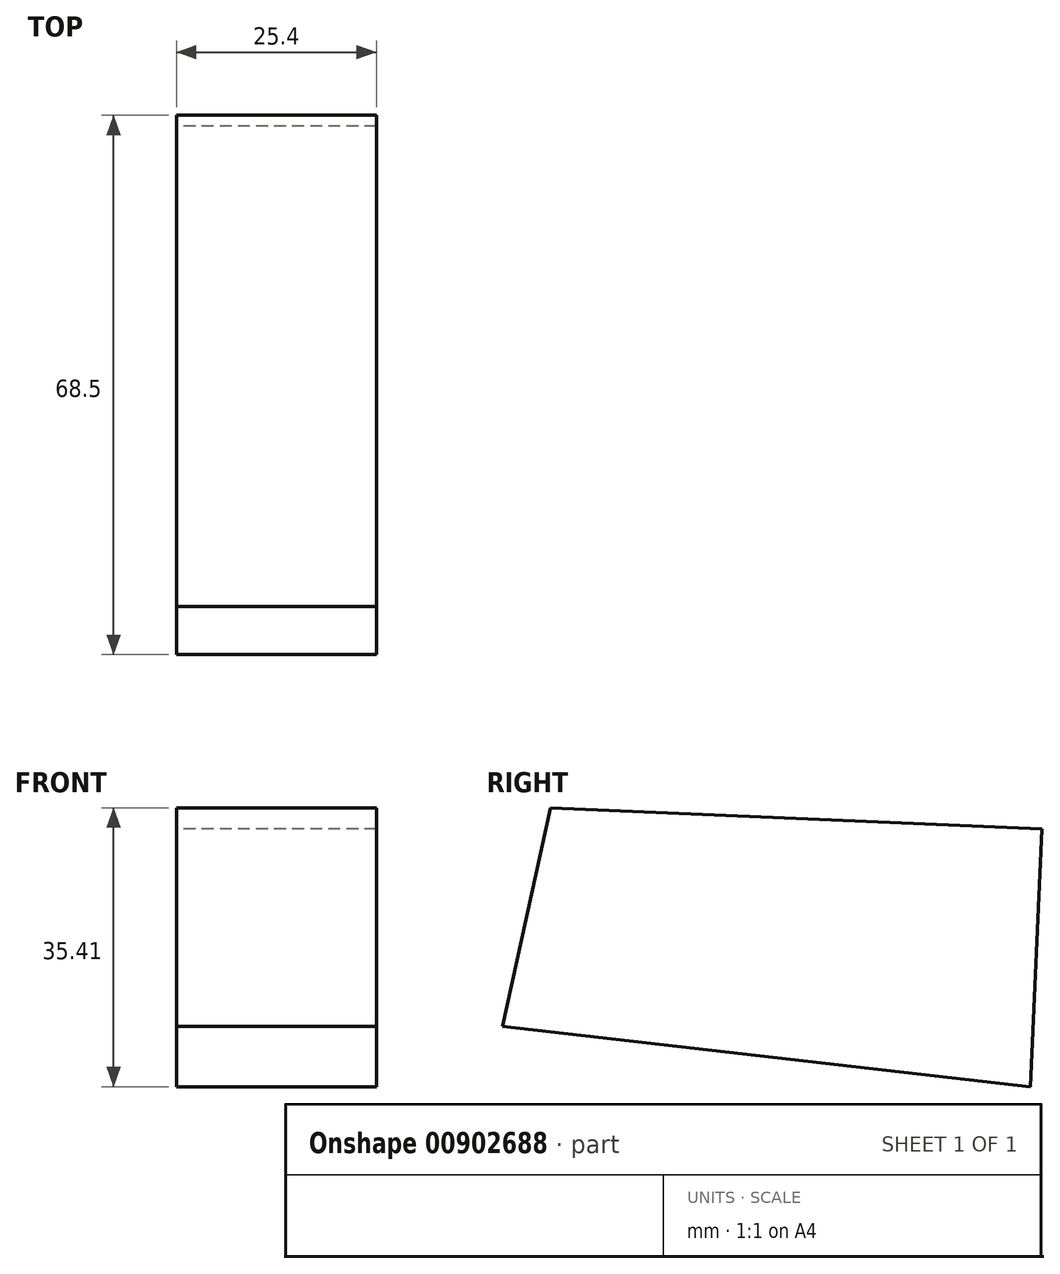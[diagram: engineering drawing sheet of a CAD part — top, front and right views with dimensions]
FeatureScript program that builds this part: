
annotation { "Feature Type Name" : "Feature", "Feature Type Description" : "" }
export const myFeature = defineFeature(function(context is Context, id is Id, definition is map)
    precondition{}
    {
        {
            var Q0;
            Q0=qCreatedBy(makeId("Right.planeOp"),FACE);
            var sketch = newSketch(context, id + "F0", { "sketchPlane" : qUnion([Q0])});
            skLineSegment(sketch, "E0", {"start": v(-40.62, 12.75) * mm, "end": v(21.79, 10.08) * mm});
            skLineSegment(sketch, "E1", {"start": v(21.79, 10.08) * mm, "end": v(20.39, -22.66) * mm});
            skLineSegment(sketch, "E2", {"start": v(20.39, -22.66) * mm, "end": v(-46.71, -15.03) * mm});
            skLineSegment(sketch, "E3", {"start": v(-46.71, -15.03) * mm, "end": v(-40.62, 12.75) * mm});
            skSolve(sketch);
        }
        {
            var Q0;
            Q0 = qSketchRegion(id + "F0", true);
            extrude(context, id + "F1", {"entities" : qUnion([Q0]), "depth" : 25.4 * mm, "offsetDistance" : 25.4 * mm});
        }
    });
